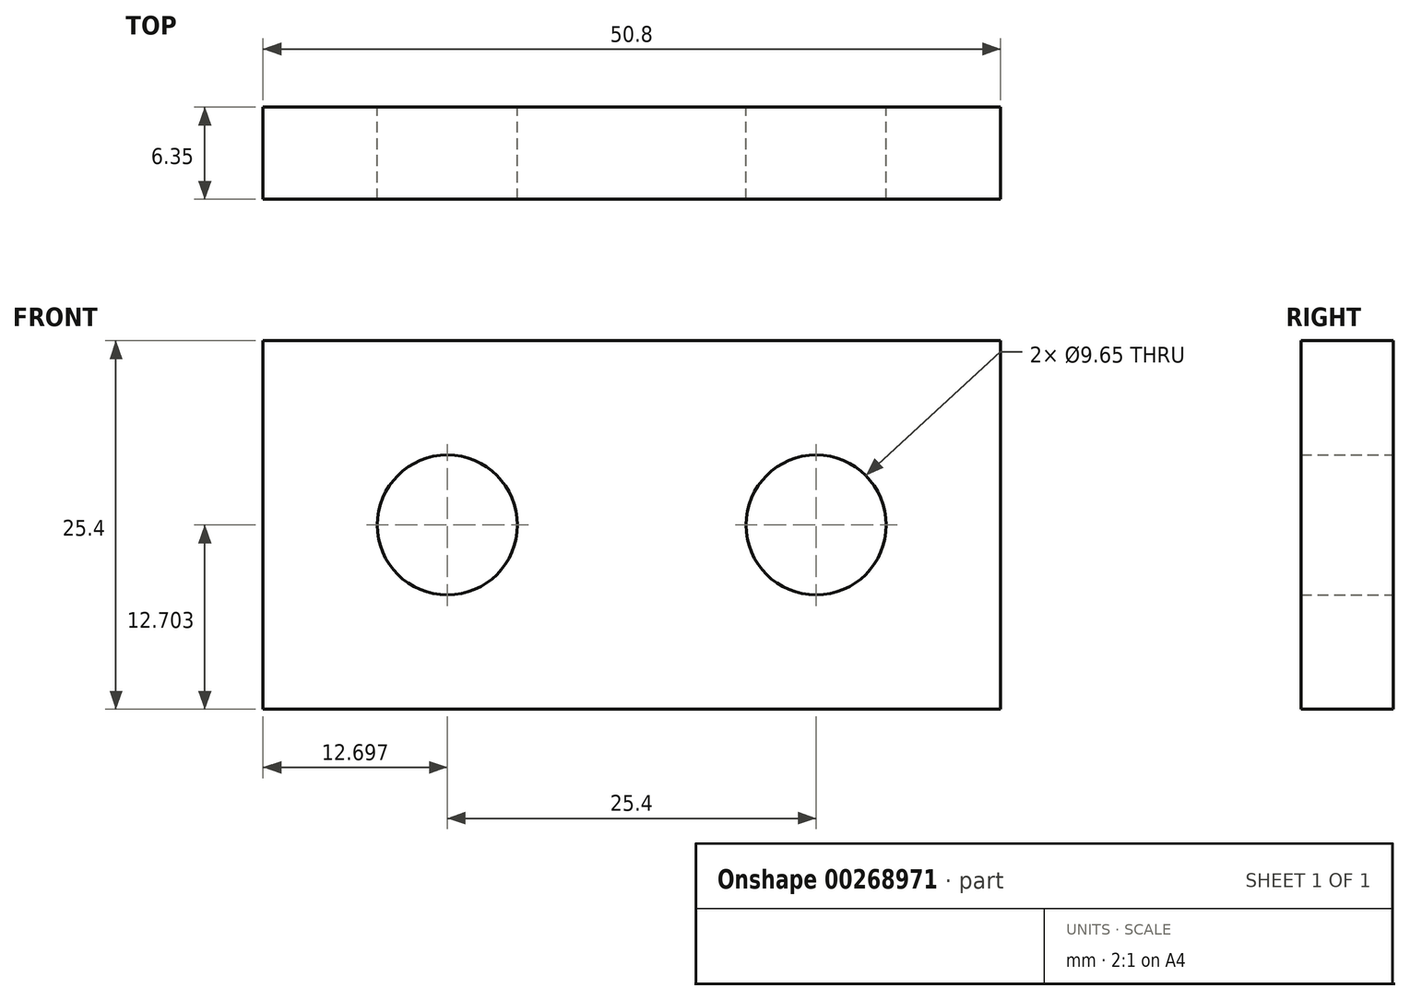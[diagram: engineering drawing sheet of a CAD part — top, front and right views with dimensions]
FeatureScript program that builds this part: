
annotation { "Feature Type Name" : "Feature", "Feature Type Description" : "" }
export const myFeature = defineFeature(function(context is Context, id is Id, definition is map)
    precondition{}
    {
        {
            var Q0;
            Q0=qCreatedBy(makeId("Front.planeOp"),FACE);
            var sketch = newSketch(context, id + "F0", { "sketchPlane" : qUnion([Q0])});
            skLineSegment(sketch, "E0.bottom", {"start": v(-76.41, 16.04) * mm, "end": v(-101.81, 16.04) * mm});
            skLineSegment(sketch, "E0.top", {"start": v(-76.41, 41.44) * mm, "end": v(-101.81, 41.44) * mm});
            skLineSegment(sketch, "E0.left", {"start": v(-76.41, 16.04) * mm, "end": v(-76.41, 41.44) * mm});
            skLineSegment(sketch, "E0.right", {"start": v(-101.81, 16.04) * mm, "end": v(-101.81, 41.44) * mm});
            skLineSegment(sketch, "E1", {"start": v(-101.81, 41.44) * mm, "end": v(-76.41, 16.04) * mm, "construction": true});
            skCircle(sketch, "E2", {"center": v(-89.11, 28.74) * mm, "radius": 4.83 * mm});
            skSolve(sketch);
        }
        {
            var Q0;
            Q0 = qSketchRegion(id + "F0", true);
            extrude(context, id + "F1", {"entities" : qUnion([Q0]), "depth" : 6.35 * mm});
        }
        {
            var Q0;
            Q0=makeQuery(id+"F1.opExtrude","SWEPT_BODY",BODY,{"disambiguationData":[OSD([sQuery(id+"F0.wireOp",EDGE,"E0.bottom"),sQuery(id+"F0.wireOp",EDGE,"E0.top"),sQuery(id+"F0.wireOp",EDGE,"E0.left"),sQuery(id+"F0.wireOp",EDGE,"E0.right"),sQuery(id+"F0.wireOp",EDGE,"E2")])]});
            var Q1;
            Q1=makeQuery(id+"F1.opExtrude","SWEPT_FACE",FACE,{"disambiguationData":[OSD([sQuery(id+"F0.wireOp",EDGE,"E0.left")])]});
            mirror(context, id + "F2", {"operationType" : NewBodyOperationType.ADD, "entities" : qUnion([Q0]), "mirrorPlane" : qUnion([Q1])});
        }
    });
